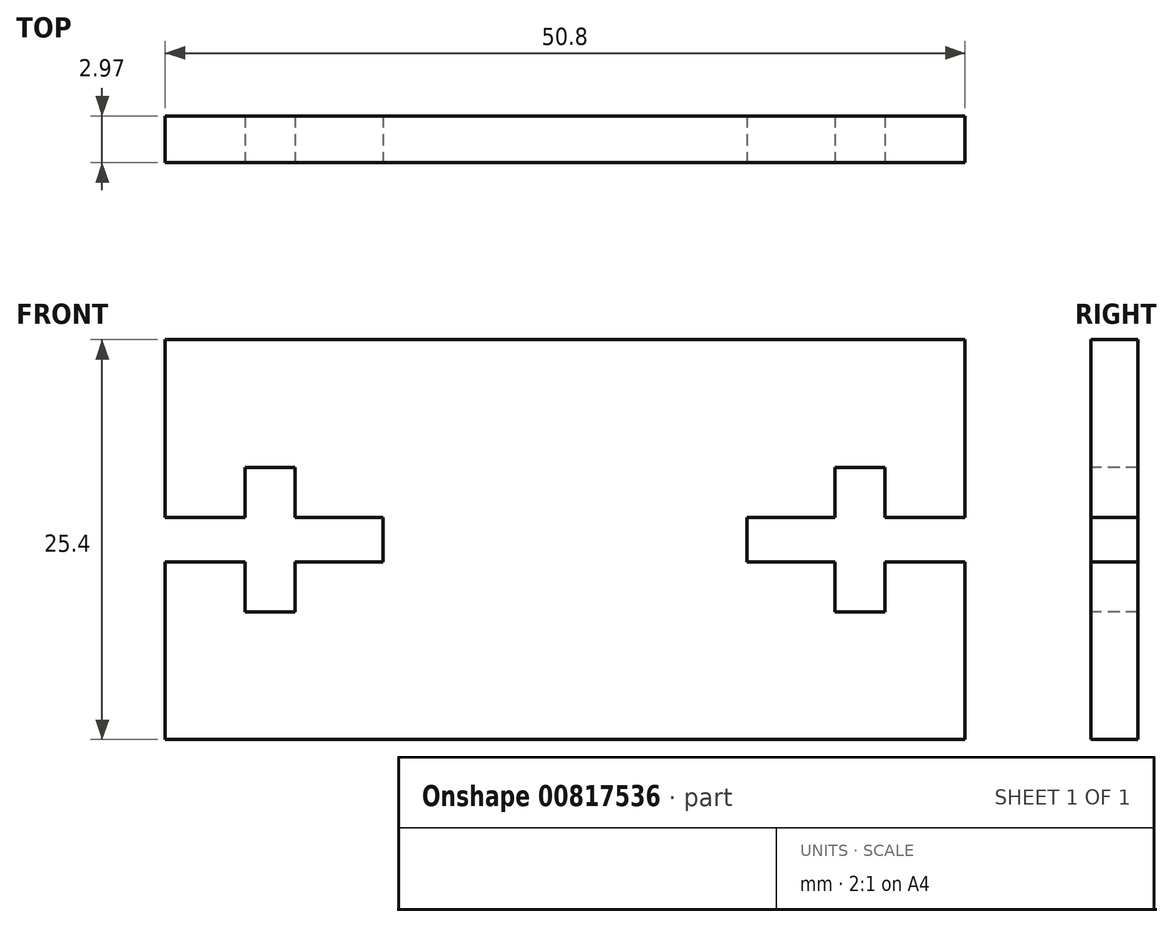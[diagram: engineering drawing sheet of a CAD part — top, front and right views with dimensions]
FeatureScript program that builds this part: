
annotation { "Feature Type Name" : "Feature", "Feature Type Description" : "" }
export const myFeature = defineFeature(function(context is Context, id is Id, definition is map)
    precondition{}
    {
        {
            var Q0;
            Q0=qCreatedBy(makeId("Front.planeOp"),FACE);
            var sketch = newSketch(context, id + "F0", { "sketchPlane" : qUnion([Q0])});
            skLineSegment(sketch, "E0", {"start": v(0, 0) * mm, "end": v(0, 25.4) * mm});
            skLineSegment(sketch, "E1", {"start": v(0, 25.4) * mm, "end": v(50.8, 25.4) * mm});
            skLineSegment(sketch, "E2", {"start": v(50.8, 25.4) * mm, "end": v(50.8, 0) * mm});
            skLineSegment(sketch, "E3", {"start": v(50.8, 0) * mm, "end": v(0, 0) * mm});
            skLineSegment(sketch, "E4", {"start": v(50.8, 14.12) * mm, "end": v(45.72, 14.12) * mm});
            skLineSegment(sketch, "E5", {"start": v(45.72, 14.12) * mm, "end": v(45.72, 17.3) * mm});
            skLineSegment(sketch, "E6", {"start": v(45.72, 17.3) * mm, "end": v(42.55, 17.3) * mm});
            skLineSegment(sketch, "E7", {"start": v(42.55, 17.3) * mm, "end": v(42.55, 14.12) * mm});
            skLineSegment(sketch, "E8", {"start": v(42.55, 14.12) * mm, "end": v(36.96, 14.12) * mm});
            skLineSegment(sketch, "E9", {"start": v(36.96, 14.12) * mm, "end": v(36.96, 11.28) * mm});
            skLineSegment(sketch, "E10", {"start": v(42.55, 8.1) * mm, "end": v(45.72, 8.1) * mm});
            skLineSegment(sketch, "E11", {"start": v(45.72, 8.1) * mm, "end": v(45.72, 11.28) * mm});
            skLineSegment(sketch, "E12", {"start": v(45.72, 11.28) * mm, "end": v(50.8, 11.28) * mm});
            skLineSegment(sketch, "E13", {"start": v(42.55, 8.1) * mm, "end": v(42.55, 11.28) * mm});
            skLineSegment(sketch, "E14", {"start": v(42.55, 11.28) * mm, "end": v(36.96, 11.28) * mm});
            skLineSegment(sketch, "E15", {"start": v(0, 14.12) * mm, "end": v(5.08, 14.12) * mm});
            skLineSegment(sketch, "E16", {"start": v(5.08, 14.12) * mm, "end": v(5.08, 17.3) * mm});
            skLineSegment(sketch, "E17", {"start": v(5.08, 17.3) * mm, "end": v(8.26, 17.3) * mm});
            skLineSegment(sketch, "E18", {"start": v(8.26, 17.3) * mm, "end": v(8.26, 14.12) * mm});
            skLineSegment(sketch, "E19", {"start": v(8.26, 14.12) * mm, "end": v(13.84, 14.12) * mm});
            skLineSegment(sketch, "E20", {"start": v(13.84, 14.12) * mm, "end": v(13.84, 11.28) * mm});
            skLineSegment(sketch, "E21", {"start": v(13.84, 11.28) * mm, "end": v(8.26, 11.28) * mm});
            skLineSegment(sketch, "E22", {"start": v(8.26, 11.28) * mm, "end": v(8.26, 8.1) * mm});
            skLineSegment(sketch, "E23", {"start": v(8.26, 8.1) * mm, "end": v(5.08, 8.1) * mm});
            skLineSegment(sketch, "E24", {"start": v(5.08, 8.1) * mm, "end": v(5.08, 11.28) * mm});
            skLineSegment(sketch, "E25", {"start": v(5.08, 11.28) * mm, "end": v(0, 11.28) * mm});
            skSolve(sketch);
        }
        {
            var Q0;
            {var subQ3=sQuery(id+"F0.wireOp",EDGE,"E1");Q0=makeQuery(id+"F0.imprint","IMPRINT",FACE,{"disambiguationData":[TD([[makeQuery(id+"F0.imprint","IMPRINT",EDGE,{"derivedFrom":subQ3}),-1.0]])]});}
            extrude(context, id + "F1", {"entities" : qUnion([Q0]), "oppositeDirection" : true, "depth" : 2.97 * mm, "offsetDistance" : 25.4 * mm});
        }
    });
